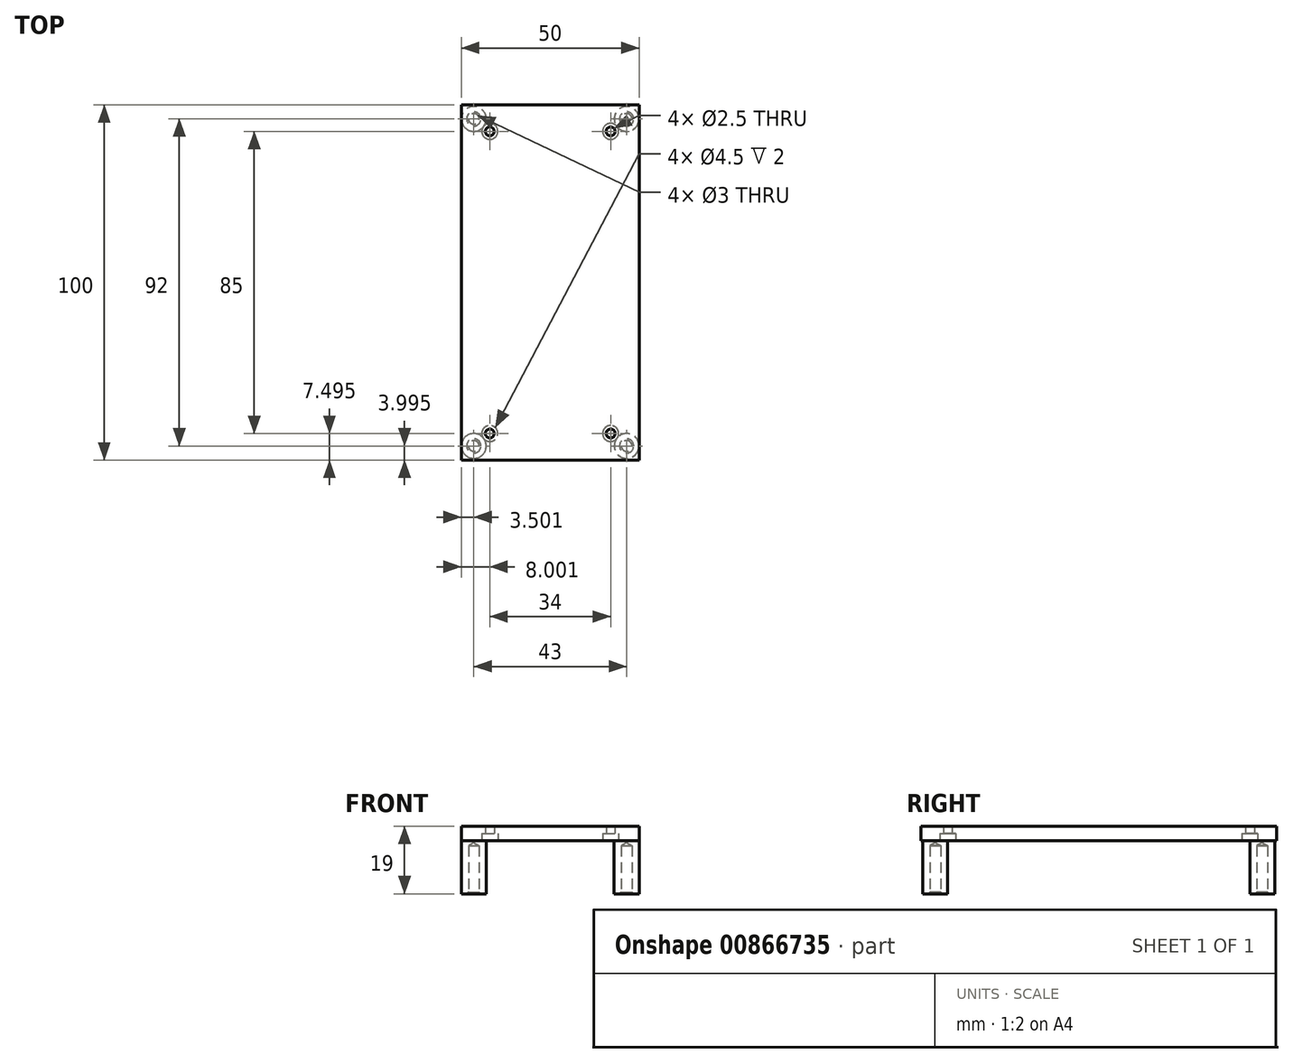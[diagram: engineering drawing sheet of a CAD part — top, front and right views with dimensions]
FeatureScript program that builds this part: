
annotation { "Feature Type Name" : "Feature", "Feature Type Description" : "" }
export const myFeature = defineFeature(function(context is Context, id is Id, definition is map)
    precondition{}
    {
        {
            assignVariable(context, id + "F0", {"name" : "RackThickness", "anyValue" : 4});
        }
        {
            assignVariable(context, id + "F1", {"name" : "PillarHeight", "anyValue" : 15});
        }
        {
            var Q0;
            Q0=qCreatedBy(makeId("Top.planeOp"),FACE);
            var sketch = newSketch(context, id + "F2", { "sketchPlane" : qUnion([Q0])});
            skLineSegment(sketch, "E0.bottom", {"start": v(-22.43, 77.5) * mm, "end": v(27.57, 77.5) * mm});
            skLineSegment(sketch, "E0.top", {"start": v(-22.43, -22.5) * mm, "end": v(27.57, -22.5) * mm});
            skLineSegment(sketch, "E0.left", {"start": v(-22.43, 77.5) * mm, "end": v(-22.43, -22.5) * mm});
            skLineSegment(sketch, "E0.right", {"start": v(27.57, 77.5) * mm, "end": v(27.57, -22.5) * mm});
            skPoint(sketch, "E1", {"position": v(-14.43, 70) * mm});
            skPoint(sketch, "E2", {"position": v(19.57, 70) * mm});
            skPoint(sketch, "E3", {"position": v(19.57, -15) * mm});
            skPoint(sketch, "E4", {"position": v(-14.43, -15) * mm});
            skPoint(sketch, "E5", {"position": v(-18.93, -18.5) * mm});
            skPoint(sketch, "E6", {"position": v(24.07, -18.5) * mm});
            skPoint(sketch, "E7", {"position": v(24.07, 73.5) * mm});
            skPoint(sketch, "E8", {"position": v(-18.93, 73.5) * mm});
            skCircle(sketch, "E9", {"center": v(-18.93, 73.5) * mm, "radius": 3.5 * mm});
            skCircle(sketch, "E10", {"center": v(-18.93, -18.5) * mm, "radius": 3.5 * mm});
            skCircle(sketch, "E11", {"center": v(24.07, -18.5) * mm, "radius": 3.5 * mm});
            skCircle(sketch, "E12", {"center": v(24.07, 73.5) * mm, "radius": 3.5 * mm});
            skSolve(sketch);
        }
        {
            var Q0;
            Q0=makeQuery(id+"F2.imprint","IMPRINT",FACE,{"disambiguationData":[TD([[makeQuery(id+"F2.imprint","IMPRINT",EDGE,{"derivedFrom":sQuery(id+"F2.wireOp",EDGE,"E0.bottom")}),-1.0]])]});
            var Q1;
            Q1=makeQuery(id+"F2.imprint","IMPRINT",FACE,{"disambiguationData":[TD([[makeQuery(id+"F2.imprint","IMPRINT",EDGE,{"derivedFrom":sQuery(id+"F2.wireOp",EDGE,"E10")}),1.0]])]});
            var Q2;
            Q2=makeQuery(id+"F2.imprint","IMPRINT",FACE,{"disambiguationData":[TD([[makeQuery(id+"F2.imprint","IMPRINT",EDGE,{"derivedFrom":sQuery(id+"F2.wireOp",EDGE,"E11")}),1.0]])]});
            var Q3;
            Q3=makeQuery(id+"F2.imprint","IMPRINT",FACE,{"disambiguationData":[TD([[makeQuery(id+"F2.imprint","IMPRINT",EDGE,{"derivedFrom":sQuery(id+"F2.wireOp",EDGE,"E9")}),1.0]])]});
            var Q4;
            Q4=makeQuery(id+"F2.imprint","IMPRINT",FACE,{"disambiguationData":[TD([[makeQuery(id+"F2.imprint","IMPRINT",EDGE,{"derivedFrom":sQuery(id+"F2.wireOp",EDGE,"E12")}),1.0]])]});
            extrude(context, id + "F3", {"entities" : qUnion([Q0, Q1, Q2, Q3, Q4]), "depth" : (getVariable(context, 'RackThickness')) * mm, "offsetDistance" : 25 * mm});
        }
        {
            var Q0;
            Q0=sQuery(id+"F2.wireOp",VERTEX,"E2");
            var Q1;
            Q1=sQuery(id+"F2.wireOp",VERTEX,"E3");
            var Q2;
            Q2=sQuery(id+"F2.wireOp",VERTEX,"E4");
            var Q3;
            Q3=sQuery(id+"F2.wireOp",VERTEX,"E1");
            var Q4;
            Q4=makeQuery(id+"F3.opExtrude","SWEPT_BODY",BODY,{"disambiguationData":[OSD([sQuery(id+"F2.wireOp",EDGE,"E0.bottom"),sQuery(id+"F2.wireOp",EDGE,"E0.top"),sQuery(id+"F2.wireOp",EDGE,"E0.left"),sQuery(id+"F2.wireOp",EDGE,"E0.right")])]});
            hole(context, id + "F4", {"style" : HoleStyle.C_BORE, "endStyle" : HoleEndStyle.THROUGH, "oppositeDirection" : true, "holeDiameter" : 2.5 * mm, "cBoreDiameter" : 4.5 * mm, "cBoreDepth" : 2 * mm, "majorDiameter" : 5 * mm, "isTappedThrough" : true, "tappedDepth" : 12 * mm, "tapClearance" : 3, "startFromSketch" : true, "locations" : qUnion([Q0, Q1, Q2, Q3]), "scope" : qUnion([Q4])});
        }
        {
            var Q0;
            Q0=makeQuery(id+"F2.imprint","IMPRINT",FACE,{"disambiguationData":[TD([[makeQuery(id+"F2.imprint","IMPRINT",EDGE,{"derivedFrom":sQuery(id+"F2.wireOp",EDGE,"E10")}),1.0]])]});
            var Q1;
            Q1=makeQuery(id+"F2.imprint","IMPRINT",FACE,{"disambiguationData":[TD([[makeQuery(id+"F2.imprint","IMPRINT",EDGE,{"derivedFrom":sQuery(id+"F2.wireOp",EDGE,"E11")}),1.0]])]});
            var Q2;
            Q2=makeQuery(id+"F2.imprint","IMPRINT",FACE,{"disambiguationData":[TD([[makeQuery(id+"F2.imprint","IMPRINT",EDGE,{"derivedFrom":sQuery(id+"F2.wireOp",EDGE,"E9")}),1.0]])]});
            var Q3;
            Q3=makeQuery(id+"F2.imprint","IMPRINT",FACE,{"disambiguationData":[TD([[makeQuery(id+"F2.imprint","IMPRINT",EDGE,{"derivedFrom":sQuery(id+"F2.wireOp",EDGE,"E12")}),1.0]])]});
            extrude(context, id + "F5", {"entities" : qUnion([Q0, Q1, Q2, Q3]), "operationType" : NewBodyOperationType.ADD, "oppositeDirection" : true, "depth" : (getVariable(context, 'PillarHeight')) * mm, "offsetDistance" : 25 * mm});
        }
        {
            var Q0;
            Q0=makeQuery(id+"F5.opExtrude","CAP_FACE",FACE,{"disambiguationData":[OSD([sQuery(id+"F2.wireOp",EDGE,"E9")])],"isStart":false});
            var sketch = newSketch(context, id + "F6", { "sketchPlane" : qUnion([Q0])});
            skPoint(sketch, "E13", {"position": v(-18.93, -73.5) * mm});
            skSolve(sketch);
        }
        {
            var Q0;
            Q0=sQuery(id+"F6.wireOp",VERTEX,"E13");
            var Q1;
            Q1=makeQuery(id+"F3.opExtrude","SWEPT_BODY",BODY,{"disambiguationData":[OSD([sQuery(id+"F2.wireOp",EDGE,"E0.bottom"),sQuery(id+"F2.wireOp",EDGE,"E0.top"),sQuery(id+"F2.wireOp",EDGE,"E0.left"),sQuery(id+"F2.wireOp",EDGE,"E0.right")])]});
            hole(context, id + "F7", {"style" : HoleStyle.C_SINK, "endStyle" : HoleEndStyle.BLIND, "holeDiameter" : 3 * mm, "cSinkDiameter" : 4 * mm, "cSinkAngle" : 90 * degree, "majorDiameter" : 5 * mm, "holeDepth" : (.9 * getVariable(context, 'PillarHeight')) * mm, "isTappedThrough" : true, "tappedDepth" : 12 * mm, "tapClearance" : 3, "startFromSketch" : true, "locations" : qUnion([Q0]), "scope" : qUnion([Q1])});
        }
        {
            var Q0;
            Q0=makeQuery(id+"F5.opExtrude","CAP_FACE",FACE,{"disambiguationData":[OSD([sQuery(id+"F2.wireOp",EDGE,"E10")])],"isStart":false});
            var sketch = newSketch(context, id + "F8", { "sketchPlane" : qUnion([Q0])});
            skPoint(sketch, "E14", {"position": v(-18.93, 18.5) * mm});
            skSolve(sketch);
        }
        {
            var Q0;
            Q0=sQuery(id+"F8.wireOp",VERTEX,"E14");
            var Q1;
            Q1=makeQuery(id+"F3.opExtrude","SWEPT_BODY",BODY,{"disambiguationData":[OSD([sQuery(id+"F2.wireOp",EDGE,"E0.bottom"),sQuery(id+"F2.wireOp",EDGE,"E0.top"),sQuery(id+"F2.wireOp",EDGE,"E0.left"),sQuery(id+"F2.wireOp",EDGE,"E0.right")])]});
            hole(context, id + "F9", {"style" : HoleStyle.C_SINK, "endStyle" : HoleEndStyle.BLIND, "holeDiameter" : 3 * mm, "cSinkDiameter" : 4 * mm, "cSinkAngle" : 90 * degree, "majorDiameter" : 5 * mm, "holeDepth" : (.9 * getVariable(context, 'PillarHeight')) * mm, "isTappedThrough" : true, "tappedDepth" : 12 * mm, "tapClearance" : 3, "startFromSketch" : true, "locations" : qUnion([Q0]), "scope" : qUnion([Q1])});
        }
        {
            var Q0;
            Q0=makeQuery(id+"F5.opExtrude","CAP_FACE",FACE,{"disambiguationData":[OSD([sQuery(id+"F2.wireOp",EDGE,"E12")])],"isStart":false});
            var sketch = newSketch(context, id + "F10", { "sketchPlane" : qUnion([Q0])});
            skPoint(sketch, "E15", {"position": v(24.07, -73.5) * mm});
            skSolve(sketch);
        }
        {
            var Q0;
            Q0=sQuery(id+"F10.wireOp",VERTEX,"E15");
            var Q1;
            Q1=makeQuery(id+"F3.opExtrude","SWEPT_BODY",BODY,{"disambiguationData":[OSD([sQuery(id+"F2.wireOp",EDGE,"E0.bottom"),sQuery(id+"F2.wireOp",EDGE,"E0.top"),sQuery(id+"F2.wireOp",EDGE,"E0.left"),sQuery(id+"F2.wireOp",EDGE,"E0.right")])]});
            hole(context, id + "F11", {"style" : HoleStyle.C_SINK, "endStyle" : HoleEndStyle.BLIND, "holeDiameter" : 3 * mm, "cSinkDiameter" : 4 * mm, "cSinkAngle" : 90 * degree, "majorDiameter" : 5 * mm, "holeDepth" : (.9 * getVariable(context, 'PillarHeight')) * mm, "isTappedThrough" : true, "tappedDepth" : 12 * mm, "tapClearance" : 3, "startFromSketch" : true, "locations" : qUnion([Q0]), "scope" : qUnion([Q1])});
        }
        {
            var Q0;
            Q0=makeQuery(id+"F5.opExtrude","CAP_FACE",FACE,{"disambiguationData":[OSD([sQuery(id+"F2.wireOp",EDGE,"E11")])],"isStart":false});
            var sketch = newSketch(context, id + "F12", { "sketchPlane" : qUnion([Q0])});
            skPoint(sketch, "E16", {"position": v(24.07, 18.5) * mm});
            skSolve(sketch);
        }
        {
            var Q0;
            Q0=sQuery(id+"F12.wireOp",VERTEX,"E16");
            var Q1;
            Q1=makeQuery(id+"F3.opExtrude","SWEPT_BODY",BODY,{"disambiguationData":[OSD([sQuery(id+"F2.wireOp",EDGE,"E0.bottom"),sQuery(id+"F2.wireOp",EDGE,"E0.top"),sQuery(id+"F2.wireOp",EDGE,"E0.left"),sQuery(id+"F2.wireOp",EDGE,"E0.right")])]});
            hole(context, id + "F13", {"style" : HoleStyle.C_SINK, "endStyle" : HoleEndStyle.BLIND, "holeDiameter" : 3 * mm, "cSinkDiameter" : 4 * mm, "cSinkAngle" : 90 * degree, "majorDiameter" : 5 * mm, "holeDepth" : (.9 * getVariable(context, 'PillarHeight')) * mm, "isTappedThrough" : true, "tappedDepth" : 12 * mm, "tapClearance" : 3, "startFromSketch" : true, "locations" : qUnion([Q0]), "scope" : qUnion([Q1])});
        }
    });
